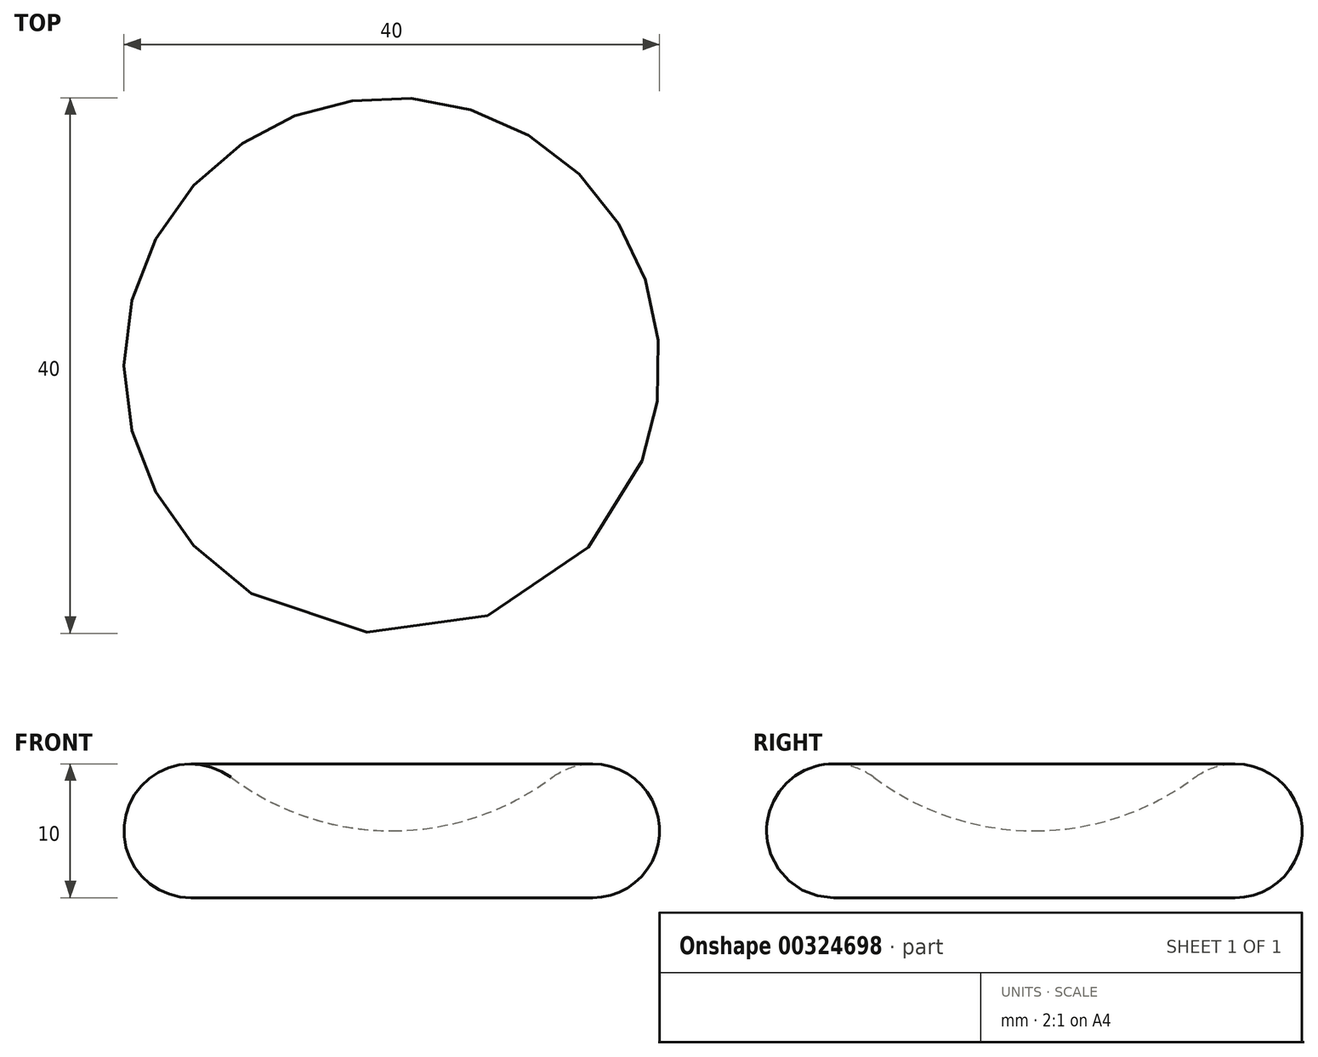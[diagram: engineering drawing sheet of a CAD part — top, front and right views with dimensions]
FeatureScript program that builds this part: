
annotation { "Feature Type Name" : "Feature", "Feature Type Description" : "" }
export const myFeature = defineFeature(function(context is Context, id is Id, definition is map)
    precondition{}
    {
        {
            var Q0;
            Q0=qCreatedBy(makeId("Front.planeOp"),FACE);
            var sketch = newSketch(context, id + "F0", { "sketchPlane" : qUnion([Q0])});
            skArc(sketch, "E0", {"start": v(-50.3, 28.32) * mm, "mid": v(-58.04, 25.9) * mm, "end": v(-53.3, 19.32) * mm});
            skArc(sketch, "E1", {"start": v(-50.3, 28.32) * mm, "mid": v(-44.63, 25.34) * mm, "end": v(-38.3, 24.32) * mm});
            skLineSegment(sketch, "E2", {"start": v(-53.3, 19.32) * mm, "end": v(-38.3, 19.32) * mm});
            skLineSegment(sketch, "E3", {"start": v(-38.3, 19.32) * mm, "end": v(-38.3, 24.32) * mm});
            skSolve(sketch);
        }
        {
            var Q0;
            Q0 = qSketchRegion(id + "F0", true);
            var Q1;
            Q1=sQuery(id+"F0.wireOp",EDGE,"E3");
            revolve(context, id + "F1", {"entities" : qUnion([Q0]), "axis" : qUnion([Q1]), "revolveType" : RevolveType.FULL});
        }
    });
